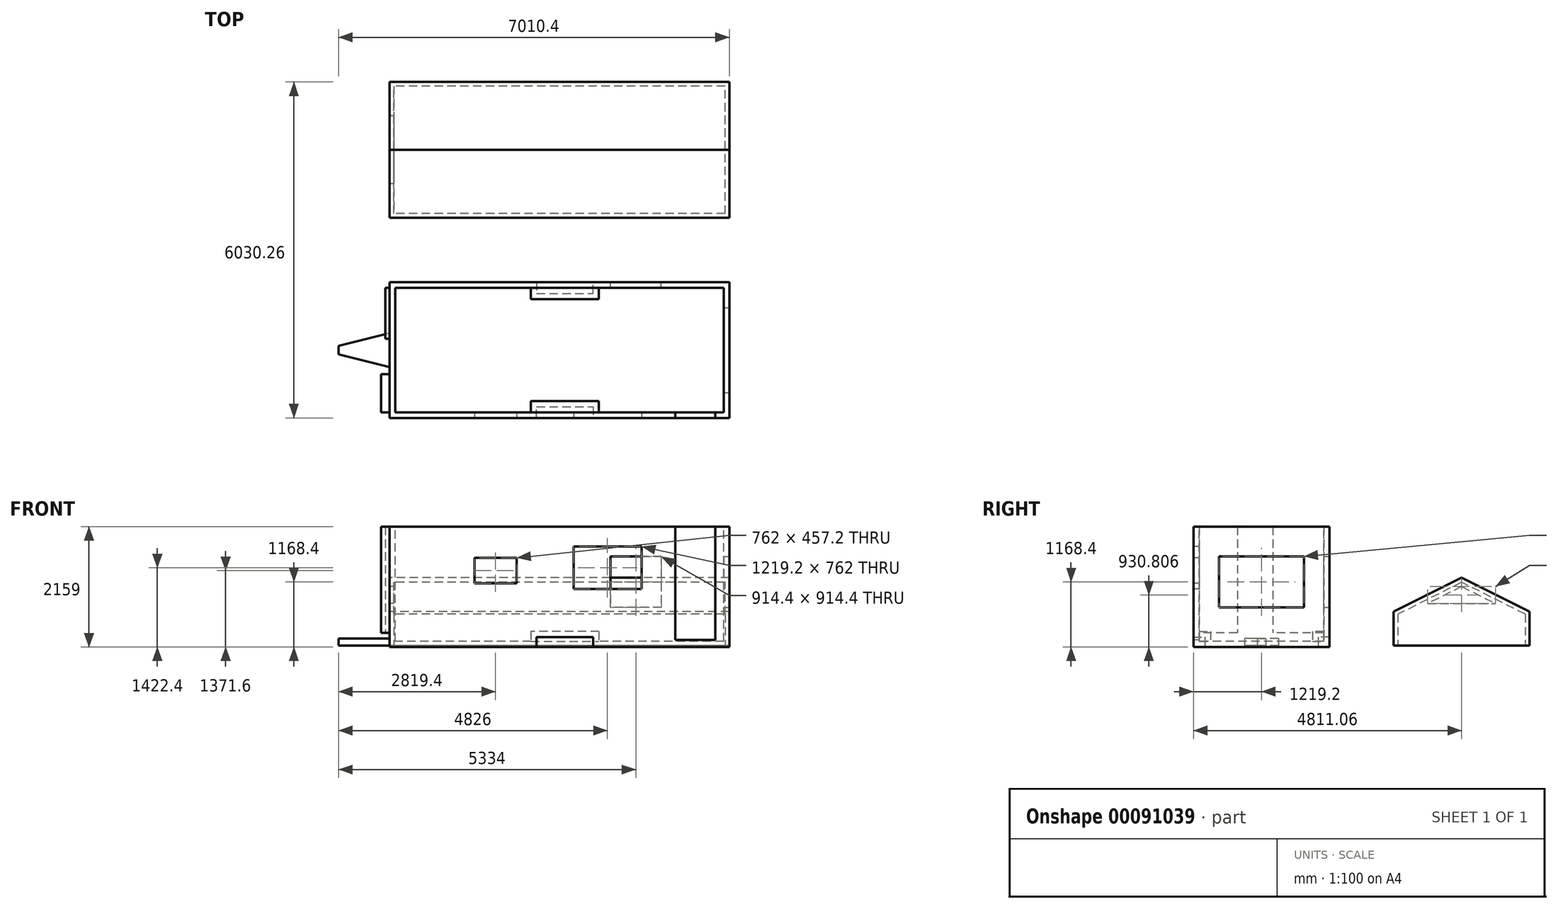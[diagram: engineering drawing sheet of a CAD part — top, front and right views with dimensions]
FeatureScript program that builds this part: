
annotation { "Feature Type Name" : "Feature", "Feature Type Description" : "" }
export const myFeature = defineFeature(function(context is Context, id is Id, definition is map)
    precondition{}
    {
        {
            var Q0;
            Q0=qCreatedBy(makeId("Top.planeOp"),FACE);
            var sketch = newSketch(context, id + "F0", { "sketchPlane" : qUnion([Q0])});
            skLineSegment(sketch, "E0.bottom", {"start": v(3048, 1219.2) * mm, "end": v(-3048, 1219.2) * mm});
            skLineSegment(sketch, "E0.top", {"start": v(3048, -1219.2) * mm, "end": v(-3048, -1219.2) * mm});
            skLineSegment(sketch, "E0.left", {"start": v(3048, 1219.2) * mm, "end": v(3048, -1219.2) * mm});
            skLineSegment(sketch, "E0.right", {"start": v(-3048, 1219.2) * mm, "end": v(-3048, -1219.2) * mm});
            skPoint(sketch, "E0.middle", {"position": v(0, 0) * mm});
            skLineSegment(sketch, "E1.bottom", {"start": v(3048, 2372.66) * mm, "end": v(-3048, 2372.66) * mm});
            skLineSegment(sketch, "E1.top", {"start": v(3048, 4811.06) * mm, "end": v(-3048, 4811.06) * mm});
            skLineSegment(sketch, "E1.left", {"start": v(3048, 2372.66) * mm, "end": v(3048, 4811.06) * mm});
            skLineSegment(sketch, "E1.right", {"start": v(-3048, 2372.66) * mm, "end": v(-3048, 4811.06) * mm});
            skLineSegment(sketch, "E2", {"start": v(1828.8, 2372.66) * mm, "end": v(1828.8, 4811.06) * mm});
            skLineSegment(sketch, "E3", {"start": v(-406.4, 2372.66) * mm, "end": v(-406.4, 4811.06) * mm});
            skSolve(sketch);
        }
        {
            var Q0;
            Q0=makeQuery(id+"F0.imprint","IMPRINT",FACE,{"disambiguationData":[TD([[makeQuery(id+"F0.imprint","IMPRINT",EDGE,{"derivedFrom":sQuery(id+"F0.wireOp",EDGE,"E0.bottom")}),1.0]])]});
            extrude(context, id + "F1", {"entities" : qUnion([Q0]), "oppositeDirection" : true, "depth" : 25.4 * mm});
        }
        {
            var Q0;
            Q0=makeQuery(id+"F0.imprint","IMPRINT",FACE,{"disambiguationData":[TD([[makeQuery(id+"F0.imprint","IMPRINT",EDGE,{"derivedFrom":sQuery(id+"F0.wireOp",EDGE,"E0.bottom")}),1.0]])]});
            extrude(context, id + "F2", {"entities" : qUnion([Q0]), "operationType" : NewBodyOperationType.ADD, "depth" : 2133.6 * mm});
        }
        {
            var Q0;
            Q0=makeQuery(id+"F1.opExtrude","CAP_FACE",FACE,{"disambiguationData":[OSD([sQuery(id+"F0.wireOp",EDGE,"E0.bottom"),sQuery(id+"F0.wireOp",EDGE,"E0.top"),sQuery(id+"F0.wireOp",EDGE,"E0.left"),sQuery(id+"F0.wireOp",EDGE,"E0.right")])],"isStart":false});
            var sketch = newSketch(context, id + "F3", { "sketchPlane" : qUnion([Q0])});
            skLineSegment(sketch, "E4", {"start": v(-406.4, 1219.2) * mm, "end": v(-406.4, 1016) * mm});
            skLineSegment(sketch, "E5", {"start": v(-406.4, 1016) * mm, "end": v(609.6, 1016) * mm});
            skLineSegment(sketch, "E6", {"start": v(609.6, 1016) * mm, "end": v(609.6, 1219.2) * mm});
            skLineSegment(sketch, "E7", {"start": v(609.6, 1219.2) * mm, "end": v(-406.4, 1219.2) * mm});
            skLineSegment(sketch, "E8", {"start": v(-406.4, -1219.2) * mm, "end": v(-406.4, -1016) * mm});
            skLineSegment(sketch, "E9", {"start": v(-406.4, -1016) * mm, "end": v(609.6, -1016) * mm});
            skLineSegment(sketch, "E10", {"start": v(609.6, -1016) * mm, "end": v(609.6, -1219.2) * mm});
            skLineSegment(sketch, "E11", {"start": v(609.6, -1219.2) * mm, "end": v(-406.4, -1219.2) * mm});
            skSolve(sketch);
        }
        {
            var Q0;
            Q0 = qSketchRegion(id + "F3", true);
            extrude(context, id + "F4", {"entities" : qUnion([Q0]), "operationType" : NewBodyOperationType.REMOVE, "oppositeDirection" : true, "depth" : 177.8 * mm});
        }
        {
            var Q0;
            Q0=makeQuery(id+"F2.opExtrude","CAP_FACE",FACE,{"disambiguationData":[OSD([sQuery(id+"F0.wireOp",EDGE,"E0.bottom"),sQuery(id+"F0.wireOp",EDGE,"E0.top"),sQuery(id+"F0.wireOp",EDGE,"E0.left"),sQuery(id+"F0.wireOp",EDGE,"E0.right")])],"isStart":false});
            shell(context, id + "F5", {"entities" : qUnion([Q0]), "thickness" : 101.6 * mm});
        }
        {
            var Q0;
            {var subQ0=sQuery(id+"F0.wireOp",EDGE,"E0.top");Q0=makeQuery(id+"F2.boolean.opBoolean","MERGE",FACE,{"derivedFrom":[makeQuery(id+"F1.opExtrude","SWEPT_FACE",FACE,{"disambiguationData":[OSD([subQ0])]}),makeQuery(id+"F2.opExtrude","SWEPT_FACE",FACE,{"disambiguationData":[OSD([subQ0])]})]});}
            var sketch = newSketch(context, id + "F6", { "sketchPlane" : qUnion([Q0])});
            skLineSegment(sketch, "E12.bottom", {"start": v(2794, 2133.6) * mm, "end": v(2082.8, 2133.6) * mm});
            skLineSegment(sketch, "E12.left", {"start": v(2794, 2133.6) * mm, "end": v(2794, 101.6) * mm});
            skLineSegment(sketch, "E12.right", {"start": v(2082.8, 2133.6) * mm, "end": v(2082.8, 101.6) * mm});
            skLineSegment(sketch, "E13", {"start": v(2082.8, 101.6) * mm, "end": v(2794, 101.6) * mm});
            skSolve(sketch);
        }
        {
            var Q0;
            Q0 = qSketchRegion(id + "F6", true);
            extrude(context, id + "F7", {"entities" : qUnion([Q0]), "operationType" : NewBodyOperationType.REMOVE, "oppositeDirection" : true, "depth" : 101.6 * mm});
        }
        {
            var Q0;
            {var subQ0=sQuery(id+"F0.wireOp",EDGE,"E0.right");Q0=makeQuery(id+"F2.boolean.opBoolean","MERGE",FACE,{"derivedFrom":[makeQuery(id+"F1.opExtrude","SWEPT_FACE",FACE,{"disambiguationData":[OSD([subQ0])]}),makeQuery(id+"F2.opExtrude","SWEPT_FACE",FACE,{"disambiguationData":[OSD([subQ0])]})]});}
            var sketch = newSketch(context, id + "F8", { "sketchPlane" : qUnion([Q0])});
            skLineSegment(sketch, "E14.bottom", {"start": v(-1117.6, 2133.6) * mm, "end": v(-203.2, 2133.6) * mm});
            skLineSegment(sketch, "E14.left", {"start": v(-1117.6, 2133.6) * mm, "end": v(-1117.6, 228.6) * mm});
            skLineSegment(sketch, "E14.right", {"start": v(-203.2, 2133.6) * mm, "end": v(-203.2, 228.6) * mm});
            skLineSegment(sketch, "E15", {"start": v(-1117.6, 228.6) * mm, "end": v(-203.2, 228.6) * mm});
            skSolve(sketch);
        }
        {
            var Q0;
            Q0=makeQuery(id+"F8.imprint","IMPRINT",FACE,{"disambiguationData":[TD([[makeQuery(id+"F8.imprint","IMPRINT",EDGE,{"derivedFrom":sQuery(id+"F8.wireOp",EDGE,"E14.bottom")}),-1.0]])]});
            extrude(context, id + "F9", {"entities" : qUnion([Q0]), "depth" : 76.2 * mm});
        }
        {
            var Q0;
            {var subQ0=sQuery(id+"F0.wireOp",EDGE,"E0.right");Q0=makeQuery(id+"F2.boolean.opBoolean","MERGE",FACE,{"derivedFrom":[makeQuery(id+"F1.opExtrude","SWEPT_FACE",FACE,{"disambiguationData":[OSD([subQ0])]}),makeQuery(id+"F2.opExtrude","SWEPT_FACE",FACE,{"disambiguationData":[OSD([subQ0])]})]});}
            var sketch = newSketch(context, id + "F10", { "sketchPlane" : qUnion([Q0])});
            skLineSegment(sketch, "E16.bottom", {"start": v(1117.6, 2133.6) * mm, "end": v(431.8, 2133.6) * mm});
            skLineSegment(sketch, "E16.left", {"start": v(1117.6, 2133.6) * mm, "end": v(1117.6, 228.6) * mm});
            skLineSegment(sketch, "E16.right", {"start": v(431.8, 2133.6) * mm, "end": v(431.8, 228.6) * mm});
            skLineSegment(sketch, "E17", {"start": v(431.8, 228.6) * mm, "end": v(1117.6, 228.6) * mm});
            skSolve(sketch);
        }
        {
            var Q0;
            Q0 = qSketchRegion(id + "F10", true);
            extrude(context, id + "F11", {"entities" : qUnion([Q0]), "depth" : 152.4 * mm});
        }
        {
            var Q0;
            {var subQ0=sQuery(id+"F0.wireOp",EDGE,"E0.top");Q0=makeQuery(id+"F2.boolean.opBoolean","MERGE",FACE,{"derivedFrom":[makeQuery(id+"F1.opExtrude","SWEPT_FACE",FACE,{"disambiguationData":[OSD([subQ0])]}),makeQuery(id+"F2.opExtrude","SWEPT_FACE",FACE,{"disambiguationData":[OSD([subQ0])]})]});}
            var sketch = newSketch(context, id + "F12", { "sketchPlane" : qUnion([Q0])});
            skLineSegment(sketch, "E18.bottom", {"start": v(-1524, 1574.8) * mm, "end": v(-762, 1574.8) * mm});
            skLineSegment(sketch, "E18.top", {"start": v(-1524, 1117.6) * mm, "end": v(-762, 1117.6) * mm});
            skLineSegment(sketch, "E18.left", {"start": v(-1524, 1574.8) * mm, "end": v(-1524, 1117.6) * mm});
            skLineSegment(sketch, "E18.right", {"start": v(-762, 1574.8) * mm, "end": v(-762, 1117.6) * mm});
            skSolve(sketch);
        }
        {
            var Q0;
            Q0 = qSketchRegion(id + "F12", true);
            extrude(context, id + "F13", {"entities" : qUnion([Q0]), "operationType" : NewBodyOperationType.REMOVE, "endBound" : BoundingType.UP_TO_NEXT, "oppositeDirection" : true, "depth" : 25.4 * mm});
        }
        {
            var Q0;
            {var subQ0=sQuery(id+"F0.wireOp",EDGE,"E0.left");Q0=makeQuery(id+"F2.boolean.opBoolean","MERGE",FACE,{"derivedFrom":[makeQuery(id+"F1.opExtrude","SWEPT_FACE",FACE,{"disambiguationData":[OSD([subQ0])]}),makeQuery(id+"F2.opExtrude","SWEPT_FACE",FACE,{"disambiguationData":[OSD([subQ0])]})]});}
            var sketch = newSketch(context, id + "F14", { "sketchPlane" : qUnion([Q0])});
            skLineSegment(sketch, "E19.bottom", {"start": v(-762, 1600.2) * mm, "end": v(762, 1600.2) * mm});
            skLineSegment(sketch, "E19.top", {"start": v(-762, 685.8) * mm, "end": v(762, 685.8) * mm});
            skLineSegment(sketch, "E19.left", {"start": v(-762, 1600.2) * mm, "end": v(-762, 685.8) * mm});
            skLineSegment(sketch, "E19.right", {"start": v(762, 1600.2) * mm, "end": v(762, 685.8) * mm});
            skLineSegment(sketch, "E20", {"start": v(0, 2133.6) * mm, "end": v(0, -25.4) * mm, "construction": true});
            skSolve(sketch);
        }
        {
            var Q0;
            Q0 = qSketchRegion(id + "F14", true);
            extrude(context, id + "F15", {"entities" : qUnion([Q0]), "operationType" : NewBodyOperationType.REMOVE, "endBound" : BoundingType.UP_TO_NEXT, "oppositeDirection" : true, "depth" : 25.4 * mm});
        }
        {
            var Q0;
            {var subQ0=sQuery(id+"F0.wireOp",EDGE,"E0.bottom");Q0=makeQuery(id+"F2.boolean.opBoolean","MERGE",FACE,{"derivedFrom":[makeQuery(id+"F1.opExtrude","SWEPT_FACE",FACE,{"disambiguationData":[OSD([subQ0])]}),makeQuery(id+"F2.opExtrude","SWEPT_FACE",FACE,{"disambiguationData":[OSD([subQ0])]})]});}
            var sketch = newSketch(context, id + "F16", { "sketchPlane" : qUnion([Q0])});
            skLineSegment(sketch, "E21.bottom", {"start": v(-1828.8, 1600.2) * mm, "end": v(-914.4, 1600.2) * mm});
            skLineSegment(sketch, "E21.top", {"start": v(-1828.8, 685.8) * mm, "end": v(-914.4, 685.8) * mm});
            skLineSegment(sketch, "E21.left", {"start": v(-1828.8, 1600.2) * mm, "end": v(-1828.8, 685.8) * mm});
            skLineSegment(sketch, "E21.right", {"start": v(-914.4, 1600.2) * mm, "end": v(-914.4, 685.8) * mm});
            skSolve(sketch);
        }
        {
            var Q0;
            Q0 = qSketchRegion(id + "F16", true);
            extrude(context, id + "F17", {"entities" : qUnion([Q0]), "operationType" : NewBodyOperationType.REMOVE, "endBound" : BoundingType.UP_TO_NEXT, "oppositeDirection" : true, "depth" : 25.4 * mm});
        }
        {
            var Q0;
            {var subQ0=sQuery(id+"F0.wireOp",EDGE,"E0.top");Q0=makeQuery(id+"F2.boolean.opBoolean","MERGE",FACE,{"derivedFrom":[makeQuery(id+"F1.opExtrude","SWEPT_FACE",FACE,{"disambiguationData":[OSD([subQ0])]}),makeQuery(id+"F2.opExtrude","SWEPT_FACE",FACE,{"disambiguationData":[OSD([subQ0])]})]});}
            var sketch = newSketch(context, id + "F18", { "sketchPlane" : qUnion([Q0])});
            skLineSegment(sketch, "E22.bottom", {"start": v(254, 1778) * mm, "end": v(1473.2, 1778) * mm});
            skLineSegment(sketch, "E22.top", {"start": v(254, 1016) * mm, "end": v(1473.2, 1016) * mm});
            skLineSegment(sketch, "E22.right", {"start": v(1473.2, 1778) * mm, "end": v(1473.2, 1016) * mm});
            skLineSegment(sketch, "E23", {"start": v(254, 1778) * mm, "end": v(254, 1016) * mm});
            skPoint(sketch, "E24.orphan", {"position": v(0, 1778) * mm});
            skSolve(sketch);
        }
        {
            var Q0;
            Q0 = qSketchRegion(id + "F18", true);
            extrude(context, id + "F19", {"entities" : qUnion([Q0]), "operationType" : NewBodyOperationType.REMOVE, "endBound" : BoundingType.UP_TO_NEXT, "oppositeDirection" : true, "depth" : 25.4 * mm});
        }
        {
            var Q0;
            {var subQ0=sQuery(id+"F0.wireOp",EDGE,"E1.right");Q0=makeQuery(id+"F0.imprint","IMPRINT",FACE,{"disambiguationData":[TD([[makeQuery(id+"F0.imprint","IMPRINT",EDGE,{"derivedFrom":subQ0}),-1.0]])]});}
            var Q1;
            {var subQ0=sQuery(id+"F0.wireOp",EDGE,"E2");Q1=makeQuery(id+"F0.imprint","IMPRINT",FACE,{"disambiguationData":[TD([[makeQuery(id+"F0.imprint","IMPRINT",EDGE,{"derivedFrom":subQ0}),1.0]])]});}
            var Q2;
            {var subQ0=sQuery(id+"F0.wireOp",EDGE,"E1.left");Q2=makeQuery(id+"F0.imprint","IMPRINT",FACE,{"disambiguationData":[TD([[makeQuery(id+"F0.imprint","IMPRINT",EDGE,{"derivedFrom":subQ0}),1.0]])]});}
            extrude(context, id + "F20", {"entities" : qUnion([Q0, Q1, Q2]), "depth" : 609.6 * mm});
        }
        {
            var Q0;
            Q0=makeQuery(id+"F20.opExtrude","SWEPT_FACE",FACE,{"disambiguationData":[OSD([sQuery(id+"F0.wireOp",EDGE,"E1.right")])]});
            var sketch = newSketch(context, id + "F21", { "sketchPlane" : qUnion([Q0])});
            skLineSegment(sketch, "E25", {"start": v(-4811.06, 609.6) * mm, "end": v(-3591.86, 1219.2) * mm});
            skPoint(sketch, "E25.endSnap0", {"position": v(-3591.86, 609.6) * mm});
            skLineSegment(sketch, "E26", {"start": v(-3591.86, 1219.2) * mm, "end": v(-2372.66, 609.6) * mm});
            skLineSegment(sketch, "E27", {"start": v(-2372.66, 609.6) * mm, "end": v(-4811.06, 609.6) * mm});
            skSolve(sketch);
        }
        {
            var Q0;
            Q0 = qSketchRegion(id + "F21", true);
            var Q1;
            Q1=makeQuery(id+"F20.opExtrude","SWEPT_FACE",FACE,{"disambiguationData":[OSD([sQuery(id+"F0.wireOp",EDGE,"E1.left")])]});
            extrude(context, id + "F22", {"entities" : qUnion([Q0]), "operationType" : NewBodyOperationType.ADD, "endBound" : BoundingType.UP_TO_SURFACE, "oppositeDirection" : true, "endBoundEntityFace" : qUnion([Q1]), "depth" : 25.4 * mm});
        }
        {
            var Q0;
            {var subQ0=sQuery(id+"F0.wireOp",EDGE,"E1.top");var subQ1=sQuery(id+"F0.wireOp",EDGE,"E1.bottom");Q0=makeQuery(id+"FxfOiSg4HxKpahv_6.boolean.opBoolean","MERGE",FACE,{"derivedFrom":[makeQuery(id+"F20.opExtrude","CAP_FACE",FACE,{"disambiguationData":[OSD([subQ1,subQ0,sQuery(id+"F0.wireOp",EDGE,"E1.left"),sQuery(id+"F0.wireOp",EDGE,"E2")])],"isStart":true}),makeQuery(id+"F20.opExtrude","CAP_FACE",FACE,{"disambiguationData":[OSD([subQ1,subQ0,sQuery(id+"F0.wireOp",EDGE,"E1.right"),sQuery(id+"F0.wireOp",EDGE,"E3")])],"isStart":true}),makeQuery(id+"FxfOiSg4HxKpahv_6.opExtrude","SWEPT_FACE",FACE,{"disambiguationData":[OSD([sQuery(id+"FImeosks4R6Lm7L_6.wireOp",EDGE,"RySwC3Iy-zk6h-osKT-uBIv-ymYqB2KaCK2P")])]})]});}
            shell(context, id + "F23", {"entities" : qUnion([Q0]), "thickness" : 76.2 * mm});
        }
        {
            var Q0;
            Q0=makeQuery(id+"F22.boolean.opBoolean","MERGE",FACE,{"derivedFrom":[makeQuery(id+"F20.opExtrude","SWEPT_FACE",FACE,{"disambiguationData":[OSD([sQuery(id+"F0.wireOp",EDGE,"E1.right")])]}),makeQuery(id+"F22.opExtrude","CAP_FACE",FACE,{"disambiguationData":[OSD([sQuery(id+"F21.wireOp",EDGE,"E25"),sQuery(id+"F21.wireOp",EDGE,"E26"),sQuery(id+"F21.wireOp",EDGE,"E27")])],"isStart":true})]});
            var sketch = newSketch(context, id + "F24", { "sketchPlane" : qUnion([Q0])});
            skLineSegment(sketch, "E28", {"start": v(-3591.86, 1057.8) * mm, "end": v(-4201.46, 753) * mm});
            skLineSegment(sketch, "E29", {"start": v(-3591.86, 1057.8) * mm, "end": v(-2982.26, 753) * mm});
            skLineSegment(sketch, "E30", {"start": v(-2982.26, 753) * mm, "end": v(-4201.46, 753) * mm});
            skSolve(sketch);
        }
        {
            var Q0;
            Q0 = qSketchRegion(id + "F24", true);
            extrude(context, id + "F25", {"entities" : qUnion([Q0]), "operationType" : NewBodyOperationType.REMOVE, "endBound" : BoundingType.UP_TO_NEXT, "oppositeDirection" : true, "depth" : 25.4 * mm});
        }
        {
            var Q0;
            Q0=makeQuery(id+"F0.imprint","IMPRINT",FACE,{"disambiguationData":[TD([[makeQuery(id+"F0.imprint","IMPRINT",EDGE,{"derivedFrom":sQuery(id+"F0.wireOp",EDGE,"E0.bottom")}),1.0]])]});
            var sketch = newSketch(context, id + "F26", { "sketchPlane" : qUnion([Q0])});
            skLineSegment(sketch, "E31", {"start": v(-5782.93, 0) * mm, "end": v(3575.5, 0) * mm, "construction": true});
            skPoint(sketch, "E31.startSnap0", {"position": v(-3048, 0) * mm});
            skPoint(sketch, "E31.endSnap0", {"position": v(-3048, 0) * mm});
            skLineSegment(sketch, "E32", {"start": v(-3962.4, -76.2) * mm, "end": v(-3962.4, 76.2) * mm});
            skLineSegment(sketch, "E33", {"start": v(-3962.4, -76.2) * mm, "end": v(-3048, -304.8) * mm});
            skLineSegment(sketch, "E34", {"start": v(-3048, -304.8) * mm, "end": v(-3048, 304.8) * mm});
            skLineSegment(sketch, "E35", {"start": v(-3048, 304.8) * mm, "end": v(-3962.4, 76.2) * mm});
            skSolve(sketch);
        }
        {
            var Q0;
            Q0 = qSketchRegion(id + "F26", true);
            extrude(context, id + "F27", {"entities" : qUnion([Q0]), "operationType" : NewBodyOperationType.ADD, "depth" : 127 * mm});
        }
    });
